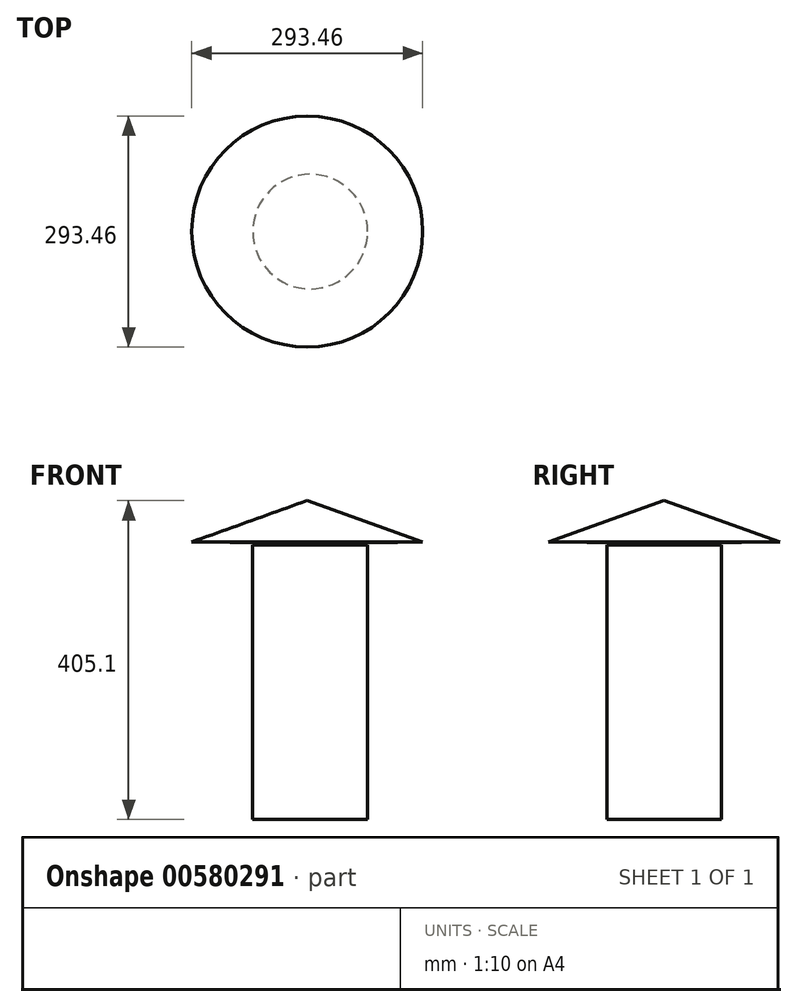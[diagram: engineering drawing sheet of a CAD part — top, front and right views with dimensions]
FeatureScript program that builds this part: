
annotation { "Feature Type Name" : "Feature", "Feature Type Description" : "" }
export const myFeature = defineFeature(function(context is Context, id is Id, definition is map)
    precondition{}
    {
        {
            var Q0;
            Q0=qCreatedBy(makeId("Top.planeOp"),FACE);
            var sketch = newSketch(context, id + "F0", { "sketchPlane" : qUnion([Q0])});
            skCircle(sketch, "E0", {"center": v(-72.89, 0) * mm, "radius": 72.89 * mm});
            skSolve(sketch);
        }
        {
            var Q0;
            Q0 = qSketchRegion(id + "F0", true);
            extrude(context, id + "F1", {"entities" : qUnion([Q0]), "depth" : 349 * mm, "offsetDistance" : 25 * mm});
        }
        {
            var Q0;
            Q0=qCreatedBy(makeId("Front.planeOp"),FACE);
            var sketch = newSketch(context, id + "F2", { "sketchPlane" : qUnion([Q0])});
            skLineSegment(sketch, "E1", {"start": v(-72.89, 0) * mm, "end": v(0, 0) * mm});
            skLineSegment(sketch, "E2", {"start": v(-76.64, 350.87) * mm, "end": v(-76.64, 405.1) * mm});
            skLineSegment(sketch, "E3", {"start": v(-76.64, 405.1) * mm, "end": v(70.09, 352.47) * mm});
            skLineSegment(sketch, "E4", {"start": v(70.09, 352.47) * mm, "end": v(-76.64, 350.87) * mm});
            skSolve(sketch);
        }
        {
            var Q0;
            Q0 = qSketchRegion(id + "F2", true);
            var Q1;
            Q1=sQuery(id+"F2.wireOp",EDGE,"E2");
            revolve(context, id + "F3", {"entities" : qUnion([Q0]), "axis" : qUnion([Q1]), "revolveType" : RevolveType.FULL});
        }
    });
